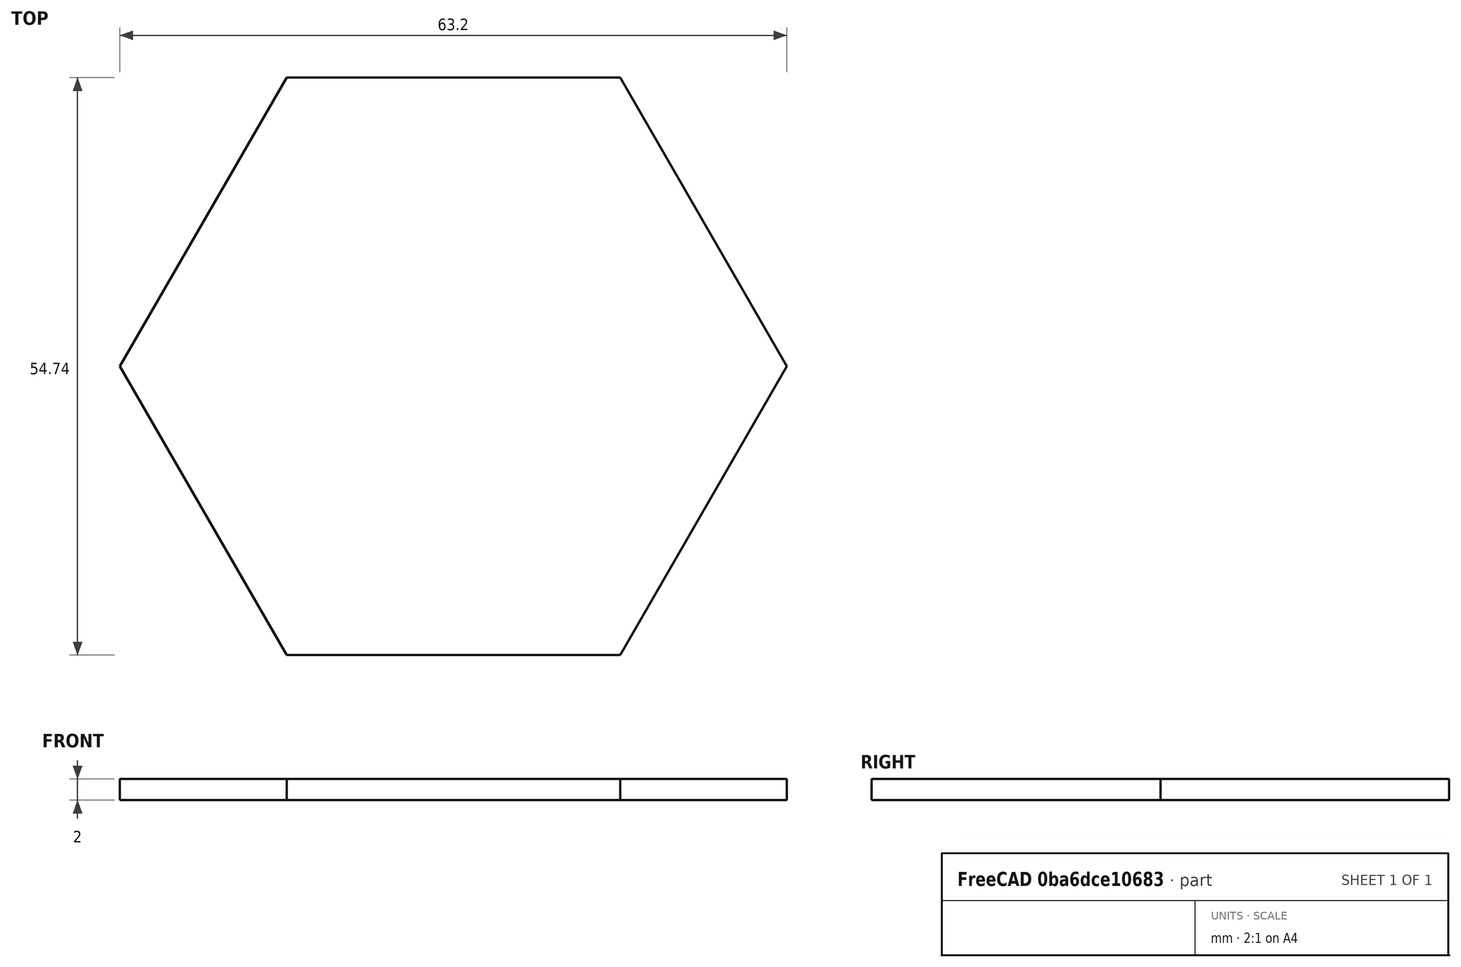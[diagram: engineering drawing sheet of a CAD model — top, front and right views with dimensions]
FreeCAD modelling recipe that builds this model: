
FCSTD DOCUMENT  (FreeCAD 1.0R39319 (Git))
Label: Top
License: All rights reserved
LicenseURL: http://en.wikipedia.org/wiki/All_rights_reserved
objects: Sketcher::SketchObject×1, PartDesign::Pad×1, PartDesign::Body×1
note: 6 computed .brp shape members not serialized (recipe doc carries the construction recipe); baked Part::Feature solids carry a one-line shape summary decoded from their .brp

FEATURE [Sketcher::SketchObject] Sketch
  ArcFitTolerance = 0
  AttachmentSupport = -> [XY_Plane]
  FullyConstrained = true
  MakeInternals = false
  MapMode = 5
  sketch-geometry (7):
    g0: LineSegment StartX=-31.6 StartY=0 StartZ=0 EndX=-15.8 EndY=-27.3664 EndZ=0
    g1: LineSegment StartX=-15.8 StartY=-27.3664 StartZ=0 EndX=15.8 EndY=-27.3664 EndZ=0
    g2: LineSegment StartX=15.8 StartY=-27.3664 StartZ=0 EndX=31.6 EndY=-6.5548e-12 EndZ=0
    g3: LineSegment StartX=31.6 StartY=-6.5548e-12 StartZ=0 EndX=15.8 EndY=27.3664 EndZ=0
    g4: LineSegment StartX=15.8 StartY=27.3664 StartZ=0 EndX=-15.8 EndY=27.3664 EndZ=0
    g5: LineSegment StartX=-15.8 StartY=27.3664 StartZ=0 EndX=-31.6 EndY=0 EndZ=0
    g6: Circle [constr] CenterX=-1e-16 CenterY=0 CenterZ=0 NormalX=0 NormalY=0 NormalZ=1 AngleXU=0 Radius=31.6
  constraints (16):
    c: Coincident(g0,g1)
    c: Coincident(g1,g2)
    c: Coincident(g2,g3)
    c: Coincident(g3,g4)
    c: Coincident(g4,g5)
    c: Coincident(g5,g0)
    c: Equal(g0, g1-g5) x5
    c: PointOnObject(g0,g6)
    c: PointOnObject(g1,g6)
    c: PointOnObject(g2,g6)
    c: PointOnObject(g3,g6)
    c: PointOnObject(g4,g6)
    c: PointOnObject(g5,g6)
    c: Coincident(g6,g-1)
    c: PointOnObject(g5,g-1)
    c: Radius(g6) = 31.6
FEATURE [PartDesign::Pad] Pad
  Direction = (0,0,1)
  Length = 2
  Length2 = 100
  Profile = -> Sketch
  Suppressed = false
  Type = 0
FEATURE [PartDesign::Body] Body
  AllowCompound = false
  Group = -> [Sketch,Pad]
  Origin = -> Origin
  Tip = -> Pad
